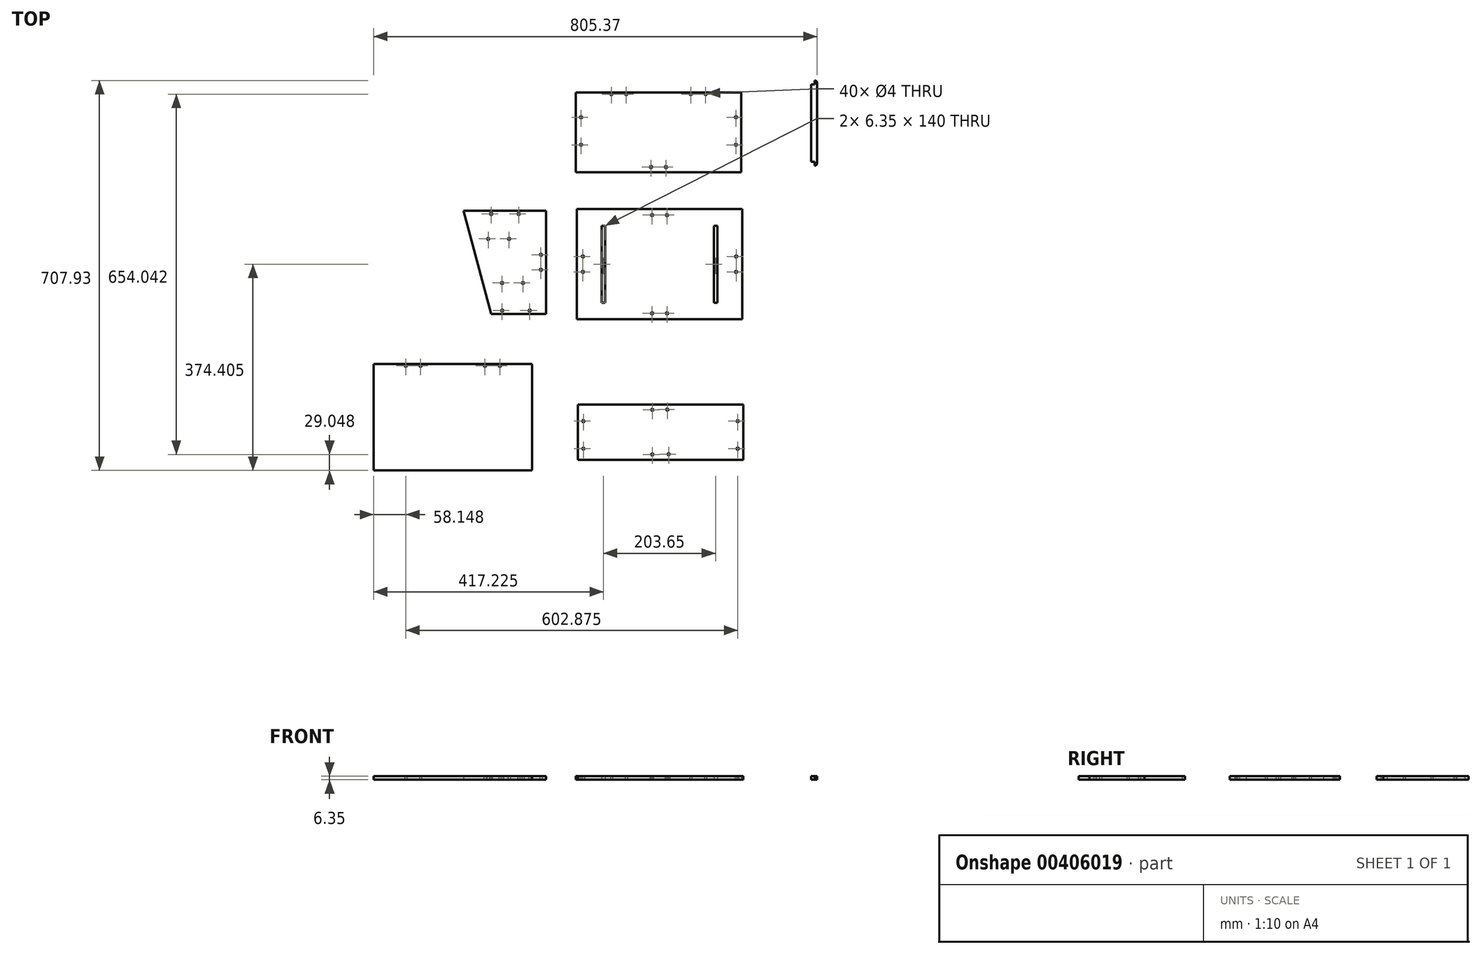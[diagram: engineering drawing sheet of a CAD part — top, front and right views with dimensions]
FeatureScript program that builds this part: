
annotation { "Feature Type Name" : "Feature", "Feature Type Description" : "" }
export const myFeature = defineFeature(function(context is Context, id is Id, definition is map)
    precondition{}
    {
        {
            var Q0;
            Q0=qCreatedBy(makeId("Top.planeOp"),FACE);
            var sketch = newSketch(context, id + "F0", { "sketchPlane" : qUnion([Q0])});
            skLineSegment(sketch, "E0.bottom", {"start": v(-121.5, 174.36) * mm, "end": v(178.5, 174.36) * mm});
            skLineSegment(sketch, "E0.top", {"start": v(-121.5, -25.64) * mm, "end": v(178.5, -25.64) * mm});
            skLineSegment(sketch, "E0.left", {"start": v(-121.5, 174.36) * mm, "end": v(-121.5, -25.64) * mm});
            skLineSegment(sketch, "E0.right", {"start": v(178.5, 174.36) * mm, "end": v(178.5, -25.64) * mm});
            skLineSegment(sketch, "E1", {"start": v(-121.5, -25.64) * mm, "end": v(0, -25.64) * mm});
            skLineSegment(sketch, "E2", {"start": v(178.5, -25.64) * mm, "end": v(57, -25.64) * mm});
            skLineSegment(sketch, "E3", {"start": v(-121.5, 174.36) * mm, "end": v(-121.5, 88.36) * mm});
            skLineSegment(sketch, "E4", {"start": v(-121.5, -25.64) * mm, "end": v(-121.5, 60.36) * mm});
            skCircle(sketch, "E5", {"center": v(-110.65, 88.36) * mm, "radius": 2 * mm});
            skCircle(sketch, "E6", {"center": v(-110.65, 60.36) * mm, "radius": 2 * mm});
            skPoint(sketch, "E7.endSnap0", {"position": v(178.5, 74.36) * mm});
            skPoint(sketch, "E8.start.orphan", {"position": v(28.5, 174.36) * mm});
            skPoint(sketch, "E7.end.orphan", {"position": v(212.54, 74.36) * mm});
            skPoint(sketch, "E7.start.orphan", {"position": v(178.5, 74.36) * mm});
            skPoint(sketch, "E9.start.orphan", {"position": v(28.5, 74.36) * mm});
            skLineSegment(sketch, "E10.MirrorCS", {"start": v(-70.15, 144.36) * mm, "end": v(-76.5, 144.36) * mm});
            skLineSegment(sketch, "E11.MirrorCS", {"start": v(-76.5, 4.36) * mm, "end": v(-70.15, 4.36) * mm});
            skLineSegment(sketch, "E12.MirrorCS", {"start": v(-76.5, 74.36) * mm, "end": v(-76.5, 144.36) * mm});
            skLineSegment(sketch, "E13.MirrorCS", {"start": v(-76.5, 74.36) * mm, "end": v(-76.5, 44.36) * mm});
            skLineSegment(sketch, "E14.MirrorCS", {"start": v(-76.5, 144.36) * mm, "end": v(-76.5, 4.36) * mm});
            skLineSegment(sketch, "E15.MirrorCS", {"start": v(-70.15, 4.36) * mm, "end": v(-70.15, 144.36) * mm});
            skLineSegment(sketch, "E16", {"start": v(303.47, 400.88) * mm, "end": v(303.47, 260.08) * mm});
            skLineSegment(sketch, "E17", {"start": v(303.47, 260.08) * mm, "end": v(309.82, 260.08) * mm});
            skLineSegment(sketch, "E18", {"start": v(309.82, 400.88) * mm, "end": v(303.47, 400.88) * mm});
            skLineSegment(sketch, "E19", {"start": v(309.82, 400.88) * mm, "end": v(309.82, 407.88) * mm});
            skLineSegment(sketch, "E20", {"start": v(309.82, 260.08) * mm, "end": v(309.82, 253.08) * mm});
            skLineSegment(sketch, "E21", {"start": v(309.82, 253.08) * mm, "end": v(309.82, 253.08) * mm});
            skLineSegment(sketch, "E22", {"start": v(314.82, 258.08) * mm, "end": v(314.82, 402.88) * mm});
            skLineSegment(sketch, "E23", {"start": v(309.82, 407.88) * mm, "end": v(309.82, 407.88) * mm});
            skPoint(sketch, "E24.visualSharp", {"position": v(314.82, 253.08) * mm});
            skArc(sketch, "E24.filletArc", {"start": v(309.82, 253.08) * mm, "mid": v(313.36, 254.55) * mm, "end": v(314.82, 258.08) * mm});
            skPoint(sketch, "E25.visualSharp", {"position": v(314.82, 407.88) * mm});
            skArc(sketch, "E25.filletArc", {"start": v(314.82, 402.88) * mm, "mid": v(313.36, 406.42) * mm, "end": v(309.82, 407.88) * mm});
            skLineSegment(sketch, "E26", {"start": v(28.5, 174.36) * mm, "end": v(28.5, 130.89) * mm});
            skPoint(sketch, "E27.start.orphan", {"position": v(0, 130.89) * mm});
            skLineSegment(sketch, "E28", {"start": v(15, 165.5) * mm, "end": v(15, 163.5) * mm});
            skLineSegment(sketch, "E29", {"start": v(15, 163.5) * mm, "end": v(17, 163.5) * mm});
            skCircle(sketch, "E30", {"center": v(15, 163.5) * mm, "radius": 2 * mm});
            skPoint(sketch, "E31.orphan", {"position": v(15, 174.36) * mm});
            skCircle(sketch, "E32", {"center": v(15, -14.8) * mm, "radius": 2 * mm});
            skPoint(sketch, "E33.trimOffspring.end.orphan", {"position": v(42, 163.5) * mm});
            skPoint(sketch, "E34.orphan", {"position": v(42, 130.89) * mm});
            skPoint(sketch, "E35.end.orphan", {"position": v(15, 130.89) * mm});
            skCircle(sketch, "E36.MirrorC", {"center": v(42, 163.5) * mm, "radius": 2 * mm});
            skCircle(sketch, "E37.MirrorC", {"center": v(42, -14.8) * mm, "radius": 2 * mm});
            skLineSegment(sketch, "E38.MirrorCS", {"start": v(127.15, 144.36) * mm, "end": v(133.5, 144.36) * mm});
            skLineSegment(sketch, "E39.MirrorCS", {"start": v(133.5, 4.36) * mm, "end": v(127.15, 4.36) * mm});
            skLineSegment(sketch, "E40.MirrorCS", {"start": v(133.5, 74.36) * mm, "end": v(133.5, 44.36) * mm});
            skLineSegment(sketch, "E41.MirrorCS", {"start": v(133.5, 144.36) * mm, "end": v(133.5, 4.36) * mm});
            skLineSegment(sketch, "E42.MirrorCS", {"start": v(133.5, 74.36) * mm, "end": v(133.5, 144.36) * mm});
            skLineSegment(sketch, "E43.MirrorCS", {"start": v(127.15, 4.36) * mm, "end": v(127.15, 144.36) * mm});
            skCircle(sketch, "E44.MirrorC", {"center": v(167.65, 60.36) * mm, "radius": 2 * mm});
            skCircle(sketch, "E45.MirrorC", {"center": v(167.65, 88.36) * mm, "radius": 2 * mm});
            skPoint(sketch, "E46.start.orphan", {"position": v(28.5, -25.64) * mm});
            skPoint(sketch, "E47.orphan", {"position": v(17, -25.64) * mm});
            skSolve(sketch);
        }
        {
            var Q0;
            Q0=qCreatedBy(makeId("Top.planeOp"),FACE);
            var sketch = newSketch(context, id + "F1", { "sketchPlane" : qUnion([Q0])});
            skLineSegment(sketch, "E48.bottom", {"start": v(-119.68, -180.5) * mm, "end": v(180.32, -180.5) * mm});
            skLineSegment(sketch, "E48.top", {"start": v(-119.68, -280.5) * mm, "end": v(180.32, -280.5) * mm});
            skLineSegment(sketch, "E48.left", {"start": v(-119.68, -180.5) * mm, "end": v(-119.68, -280.5) * mm});
            skLineSegment(sketch, "E48.right", {"start": v(180.32, -180.5) * mm, "end": v(180.32, -280.5) * mm});
            skLineSegment(sketch, "E49", {"start": v(-119.68, -180.5) * mm, "end": v(1.82, -180.5) * mm});
            skLineSegment(sketch, "E50", {"start": v(180.32, -180.5) * mm, "end": v(58.82, -180.5) * mm});
            skLineSegment(sketch, "E51", {"start": v(-119.68, -180.5) * mm, "end": v(-119.68, -210.5) * mm});
            skLineSegment(sketch, "E52", {"start": v(-119.68, -180.5) * mm, "end": v(-119.68, -260.5) * mm});
            skCircle(sketch, "E53", {"center": v(-109.83, -210.5) * mm, "radius": 2 * mm});
            skCircle(sketch, "E54", {"center": v(-109.83, -260.5) * mm, "radius": 2 * mm});
            skPoint(sketch, "E55.endSnap0", {"position": v(180.32, -230.5) * mm});
            skPoint(sketch, "E55.start.orphan", {"position": v(180.32, -230.5) * mm});
            skPoint(sketch, "E56.start.orphan", {"position": v(30.32, -280.5) * mm});
            skPoint(sketch, "E57.center.orphan", {"position": v(28.82, -190) * mm});
            skPoint(sketch, "E58.center.orphan", {"position": v(1.82, -190) * mm});
            skLineSegment(sketch, "E59", {"start": v(28.82, -180.5) * mm, "end": v(15.32, -180.5) * mm});
            skCircle(sketch, "E60", {"center": v(15.32, -190) * mm, "radius": 2 * mm});
            skCircle(sketch, "E61", {"center": v(15.32, -271) * mm, "radius": 2 * mm});
            skCircle(sketch, "E62.MirrorC", {"center": v(42.6, -189.6) * mm, "radius": 2 * mm});
            skCircle(sketch, "E63.MirrorC", {"center": v(45.03, -270.56) * mm, "radius": 2 * mm});
            skLineSegment(sketch, "E64", {"start": v(30.32, -280.5) * mm, "end": v(30.32, -182.54) * mm});
            skPoint(sketch, "E64.endSnap0", {"position": v(30.32, -180.5) * mm});
            skCircle(sketch, "E65.MirrorC", {"center": v(170.47, -210.5) * mm, "radius": 2 * mm});
            skCircle(sketch, "E66.MirrorC", {"center": v(170.47, -260.5) * mm, "radius": 2 * mm});
            skSolve(sketch);
        }
        {
            var Q0;
            Q0=qCreatedBy(makeId("Top.planeOp"),FACE);
            var sketch = newSketch(context, id + "F2", { "sketchPlane" : qUnion([Q0])});
            skLineSegment(sketch, "E67.bottom", {"start": v(-327.3, 171.56) * mm, "end": v(-177.3, 171.56) * mm});
            skLineSegment(sketch, "E67.top", {"start": v(-277.3, -15.74) * mm, "end": v(-177.3, -15.74) * mm});
            skLineSegment(sketch, "E67.right", {"start": v(-177.3, 171.56) * mm, "end": v(-177.3, -15.74) * mm});
            skLineSegment(sketch, "E68", {"start": v(-177.3, -15.74) * mm, "end": v(-277.3, -15.74) * mm});
            skLineSegment(sketch, "E69", {"start": v(-277.3, -15.74) * mm, "end": v(-327.3, 171.56) * mm});
            skPoint(sketch, "E70.orphan", {"position": v(-327.3, -15.74) * mm});
            skLineSegment(sketch, "E71", {"start": v(-177.3, 171.56) * mm, "end": v(-244.6, 171.56) * mm});
            skLineSegment(sketch, "E72", {"start": v(-177.3, 171.56) * mm, "end": v(-282.6, 171.56) * mm});
            skLineSegment(sketch, "E73", {"start": v(-177.3, 171.56) * mm, "end": v(-208.6, 171.56) * mm});
            skLineSegment(sketch, "E74", {"start": v(-177.3, 171.56) * mm, "end": v(-246.6, 171.56) * mm});
            skCircle(sketch, "E75", {"center": v(-244.6, 120.26) * mm, "radius": 2 * mm});
            skCircle(sketch, "E76", {"center": v(-282.6, 120.26) * mm, "radius": 2 * mm});
            skLineSegment(sketch, "E77", {"start": v(-177.3, 171.56) * mm, "end": v(-177.3, 91.56) * mm});
            skLineSegment(sketch, "E78", {"start": v(-177.3, -15.74) * mm, "end": v(-177.3, 64.26) * mm});
            skCircle(sketch, "E79", {"center": v(-186.8, 91.56) * mm, "radius": 2 * mm});
            skCircle(sketch, "E80", {"center": v(-186.8, 64.26) * mm, "radius": 2 * mm});
            skLineSegment(sketch, "E81", {"start": v(-177.3, -15.74) * mm, "end": v(-207.3, -15.74) * mm});
            skLineSegment(sketch, "E82", {"start": v(-177.3, -15.74) * mm, "end": v(-257.3, -15.74) * mm});
            skCircle(sketch, "E83", {"center": v(-257.3, -9.74) * mm, "radius": 2 * mm});
            skCircle(sketch, "E84", {"center": v(-207.3, -9.74) * mm, "radius": 2 * mm});
            skLineSegment(sketch, "E85", {"start": v(-177.3, 171.56) * mm, "end": v(-227.3, 171.56) * mm});
            skLineSegment(sketch, "E86", {"start": v(-177.3, 171.56) * mm, "end": v(-277.3, 171.56) * mm});
            skCircle(sketch, "E87", {"center": v(-277.3, 165.56) * mm, "radius": 2 * mm});
            skCircle(sketch, "E88", {"center": v(-227.3, 165.56) * mm, "radius": 2 * mm});
            skLineSegment(sketch, "E89.bottom", {"start": v(468.15, 178.9) * mm, "end": v(618.15, 178.9) * mm});
            skLineSegment(sketch, "E89.top", {"start": v(518.15, -8.4) * mm, "end": v(618.15, -8.4) * mm});
            skLineSegment(sketch, "E89.right", {"start": v(618.15, 178.9) * mm, "end": v(618.15, -8.4) * mm});
            skLineSegment(sketch, "E90", {"start": v(618.15, -8.4) * mm, "end": v(518.15, -8.4) * mm});
            skLineSegment(sketch, "E91", {"start": v(518.15, -8.4) * mm, "end": v(468.15, 178.9) * mm});
            skPoint(sketch, "E92.orphan", {"position": v(468.15, -8.4) * mm});
            skLineSegment(sketch, "E93", {"start": v(618.15, 178.9) * mm, "end": v(550.85, 178.9) * mm});
            skLineSegment(sketch, "E94", {"start": v(618.15, 178.9) * mm, "end": v(512.85, 178.9) * mm});
            skLineSegment(sketch, "E95", {"start": v(618.15, 178.9) * mm, "end": v(586.85, 178.9) * mm});
            skLineSegment(sketch, "E96", {"start": v(618.15, 178.9) * mm, "end": v(548.85, 178.9) * mm});
            skLineSegment(sketch, "E97", {"start": v(618.15, 178.9) * mm, "end": v(618.15, 98.9) * mm});
            skLineSegment(sketch, "E98", {"start": v(618.15, -8.4) * mm, "end": v(618.15, 71.6) * mm});
            skCircle(sketch, "E99", {"center": v(608.65, 98.9) * mm, "radius": 2 * mm});
            skCircle(sketch, "E100", {"center": v(608.65, 71.6) * mm, "radius": 2 * mm});
            skLineSegment(sketch, "E101", {"start": v(618.15, -8.4) * mm, "end": v(588.15, -8.4) * mm});
            skLineSegment(sketch, "E102", {"start": v(618.15, -8.4) * mm, "end": v(538.15, -8.4) * mm});
            skCircle(sketch, "E103", {"center": v(538.15, 3.95) * mm, "radius": 2 * mm});
            skCircle(sketch, "E104", {"center": v(588.15, 3.95) * mm, "radius": 2 * mm});
            skLineSegment(sketch, "E105", {"start": v(618.15, 178.9) * mm, "end": v(568.15, 178.9) * mm});
            skLineSegment(sketch, "E106", {"start": v(618.15, 178.9) * mm, "end": v(518.15, 178.9) * mm});
            skCircle(sketch, "E107", {"center": v(518.15, 166.55) * mm, "radius": 2 * mm});
            skCircle(sketch, "E108", {"center": v(568.15, 166.55) * mm, "radius": 2 * mm});
            skPoint(sketch, "E109.center.orphan", {"position": v(512.85, 127.6) * mm});
            skPoint(sketch, "E110.center.orphan", {"position": v(550.85, 127.6) * mm});
            skPoint(sketch, "E111.center.orphan", {"position": v(548.85, 37.6) * mm});
            skPoint(sketch, "E112.center.orphan", {"position": v(586.85, 37.6) * mm});
            skCircle(sketch, "E113", {"center": v(-257.48, 40.26) * mm, "radius": 2 * mm});
            skCircle(sketch, "E114", {"center": v(-219.48, 40.26) * mm, "radius": 2 * mm});
            skPoint(sketch, "E115.start.orphan", {"position": v(-209.48, 30.26) * mm});
            skPoint(sketch, "E116.start.orphan", {"position": v(-247.48, 30.26) * mm});
            skSolve(sketch);
        }
        {
            var Q0;
            Q0=qCreatedBy(makeId("Top.planeOp"),FACE);
            var sketch = newSketch(context, id + "F3", { "sketchPlane" : qUnion([Q0])});
            skLineSegment(sketch, "E117.bottom", {"start": v(-123.38, 386.04) * mm, "end": v(176.62, 386.04) * mm});
            skLineSegment(sketch, "E117.top", {"start": v(-123.38, 241.04) * mm, "end": v(176.62, 241.04) * mm});
            skLineSegment(sketch, "E117.left", {"start": v(-123.38, 386.04) * mm, "end": v(-123.38, 241.04) * mm});
            skLineSegment(sketch, "E117.right", {"start": v(176.62, 386.04) * mm, "end": v(176.62, 241.04) * mm});
            skLineSegment(sketch, "E118", {"start": v(-123.38, 386.04) * mm, "end": v(-123.38, 336.04) * mm});
            skLineSegment(sketch, "E119", {"start": v(-123.38, 386.04) * mm, "end": v(-123.38, 286.04) * mm});
            skLineSegment(sketch, "E120", {"start": v(-123.38, 241.04) * mm, "end": v(-1.88, 241.04) * mm});
            skLineSegment(sketch, "E121", {"start": v(176.62, 241.04) * mm, "end": v(55.12, 241.04) * mm});
            skPoint(sketch, "E122.start.orphan", {"position": v(26.62, 386.04) * mm});
            skLineSegment(sketch, "E123", {"start": v(-123.38, 386.04) * mm, "end": v(-46.88, 386.04) * mm});
            skLineSegment(sketch, "E124", {"start": v(-123.38, 386.04) * mm, "end": v(-19.88, 386.04) * mm});
            skLineSegment(sketch, "E125", {"start": v(-123.38, 241.04) * mm, "end": v(-123.38, 291.04) * mm});
            skLineSegment(sketch, "E126", {"start": v(-123.38, 241.04) * mm, "end": v(-123.38, 341.04) * mm});
            skCircle(sketch, "E127", {"center": v(-114.03, 341.04) * mm, "radius": 2 * mm});
            skCircle(sketch, "E128", {"center": v(-114.03, 291.04) * mm, "radius": 2 * mm});
            skPoint(sketch, "E129.center.orphan", {"position": v(-19.88, 383.04) * mm});
            skPoint(sketch, "E130.center.orphan", {"position": v(-31.88, 383.04) * mm});
            skLineSegment(sketch, "E131", {"start": v(-31.88, 381.04) * mm, "end": v(-31.88, 386.04) * mm});
            skCircle(sketch, "E132", {"center": v(-31.88, 383.04) * mm, "radius": 2 * mm});
            skLineSegment(sketch, "E133", {"start": v(-31.88, 383.04) * mm, "end": v(-33.88, 383.04) * mm});
            skCircle(sketch, "E134", {"center": v(-58.88, 383.04) * mm, "radius": 2 * mm});
            skLineSegment(sketch, "E135.trimOffspring", {"start": v(-56.88, 383.04) * mm, "end": v(-58.88, 383.04) * mm});
            skPoint(sketch, "E136.end.orphan", {"position": v(-4.88, 383.04) * mm});
            skPoint(sketch, "E136.start.orphan", {"position": v(-4.88, 386.04) * mm});
            skPoint(sketch, "E137.center.orphan", {"position": v(25.12, 250.54) * mm});
            skPoint(sketch, "E138.center.orphan", {"position": v(-1.88, 250.54) * mm});
            skLineSegment(sketch, "E139", {"start": v(26.62, 241.04) * mm, "end": v(13.12, 241.04) * mm});
            skLineSegment(sketch, "E140", {"start": v(13.12, 241.04) * mm, "end": v(40.12, 241.04) * mm});
            skPoint(sketch, "E141.end.orphan", {"position": v(40.12, 250.54) * mm});
            skCircle(sketch, "E142", {"center": v(13.12, 250.54) * mm, "radius": 2 * mm});
            skCircle(sketch, "E143", {"center": v(40.12, 250.54) * mm, "radius": 2 * mm});
            skPoint(sketch, "E144.MirrorC.center.orphan", {"position": v(167.27, 341.04) * mm});
            skCircle(sketch, "E145.MirrorC", {"center": v(85.12, 383.04) * mm, "radius": 2 * mm});
            skCircle(sketch, "E146.MirrorC", {"center": v(112.12, 383.04) * mm, "radius": 2 * mm});
            skCircle(sketch, "E147.MirrorC", {"center": v(167.27, 341.04) * mm, "radius": 2 * mm});
            skCircle(sketch, "E148.MirrorC", {"center": v(167.27, 291.04) * mm, "radius": 2 * mm});
            skSolve(sketch);
        }
        {
            var Q0;
            Q0=makeQuery(id+"F1.imprint","IMPRINT",FACE,{"disambiguationData":[TD([[makeQuery(id+"F1.imprint","IMPRINT",EDGE,{"derivedFrom":sQuery(id+"F1.wireOp",EDGE,"E48.bottom")}),-1.0]])]});
            var Q1;
            Q1=makeQuery(id+"F0.imprint","IMPRINT",FACE,{"disambiguationData":[TD([[makeQuery(id+"F0.imprint","IMPRINT",EDGE,{"derivedFrom":sQuery(id+"F0.wireOp",EDGE,"E0.bottom")}),-1.0]])]});
            var Q2;
            Q2=makeQuery(id+"F2.imprint","IMPRINT",FACE,{"disambiguationData":[TD([[makeQuery(id+"F2.imprint","IMPRINT",EDGE,{"derivedFrom":sQuery(id+"F2.wireOp",EDGE,"51ad1dc0-d7a0-4be4-aa9f-00c25df09339.bottom")}),-1.0]])]});
            var Q3;
            {var subQ4=sQuery(id+"F3.wireOp",EDGE,"E117.bottom");Q3=makeQuery(id+"F3.imprint","IMPRINT",FACE,{"disambiguationData":[TD([[makeQuery(id+"F3.imprint","IMPRINT",EDGE,{"derivedFrom":subQ4}),-1.0]])]});}
            var Q4;
            Q4=makeQuery(id+"F2.imprint","IMPRINT",FACE,{"disambiguationData":[TD([[makeQuery(id+"F2.imprint","IMPRINT",EDGE,{"derivedFrom":sQuery(id+"F2.wireOp",EDGE,"E67.bottom")}),-1.0]])]});
            extrude(context, id + "F4", {"entities" : qUnion([Q0, Q1, Q2, Q3, Q4]), "depth" : 6.35 * mm});
        }
        {
            var Q0;
            Q0 = qSketchRegion(id + "F0", true);
            var Q1;
            Q1 = qSketchRegion(id + "F6", true);
            extrude(context, id + "F5", {"entities" : qUnion([Q0, Q1]), "operationType" : NewBodyOperationType.ADD, "depth" : 6.35 * mm});
        }
        {
            var Q0;
            Q0=qCreatedBy(makeId("Top.planeOp"),FACE);
            var sketch = newSketch(context, id + "F6", { "sketchPlane" : qUnion([Q0])});
            skLineSegment(sketch, "E149.bottom", {"start": v(-490.55, -107.05) * mm, "end": v(-203.25, -107.05) * mm});
            skLineSegment(sketch, "E149.top", {"start": v(-490.55, -300.05) * mm, "end": v(-203.25, -300.05) * mm});
            skLineSegment(sketch, "E149.left", {"start": v(-490.55, -107.05) * mm, "end": v(-490.55, -300.05) * mm});
            skLineSegment(sketch, "E149.right", {"start": v(-203.25, -107.05) * mm, "end": v(-203.25, -300.05) * mm});
            skLineSegment(sketch, "E150", {"start": v(-346.9, -107.05) * mm, "end": v(-378.4, -107.05) * mm});
            skLineSegment(sketch, "E151", {"start": v(-346.9, -107.05) * mm, "end": v(-405.4, -107.05) * mm});
            skPoint(sketch, "E152.center.orphan", {"position": v(-420.4, -110.05) * mm});
            skPoint(sketch, "E153.center.orphan", {"position": v(-393.4, -110.05) * mm});
            skPoint(sketch, "E154.MirrorC.center.orphan", {"position": v(-330.4, -110.05) * mm});
            skPoint(sketch, "E155.MirrorC.center.orphan", {"position": v(-303.4, -110.05) * mm});
            skPoint(sketch, "E156.endSnap0", {"position": v(-376.15, -129.13) * mm});
            skCircle(sketch, "E157", {"center": v(-432.4, -110.05) * mm, "radius": 2 * mm});
            skCircle(sketch, "E158", {"center": v(-405.4, -110.05) * mm, "radius": 2 * mm});
            skPoint(sketch, "E156.end.orphan", {"position": v(-432.4, -129.13) * mm});
            skPoint(sketch, "E159.orphan", {"position": v(-405.4, -129.13) * mm});
            skPoint(sketch, "E160.start.orphan", {"position": v(-346.9, -129.13) * mm});
            skCircle(sketch, "E161.MirrorC", {"center": v(-288.4, -110.05) * mm, "radius": 2 * mm});
            skCircle(sketch, "E162.MirrorC", {"center": v(-261.4, -110.05) * mm, "radius": 2 * mm});
            skPoint(sketch, "E163.end.orphan", {"position": v(-432.4, -107.05) * mm});
            skPoint(sketch, "E164.start.orphan", {"position": v(-346.9, -300.05) * mm});
            skSolve(sketch);
        }
        {
            var Q0;
            Q0=makeQuery(id+"F6.imprint","IMPRINT",FACE,{"disambiguationData":[TD([[makeQuery(id+"F6.imprint","IMPRINT",EDGE,{"derivedFrom":sQuery(id+"F6.wireOp",EDGE,"E149.top")}),1.0]])]});
            extrude(context, id + "F7", {"entities" : qUnion([Q0]), "depth" : 6.35 * mm});
        }
    });
